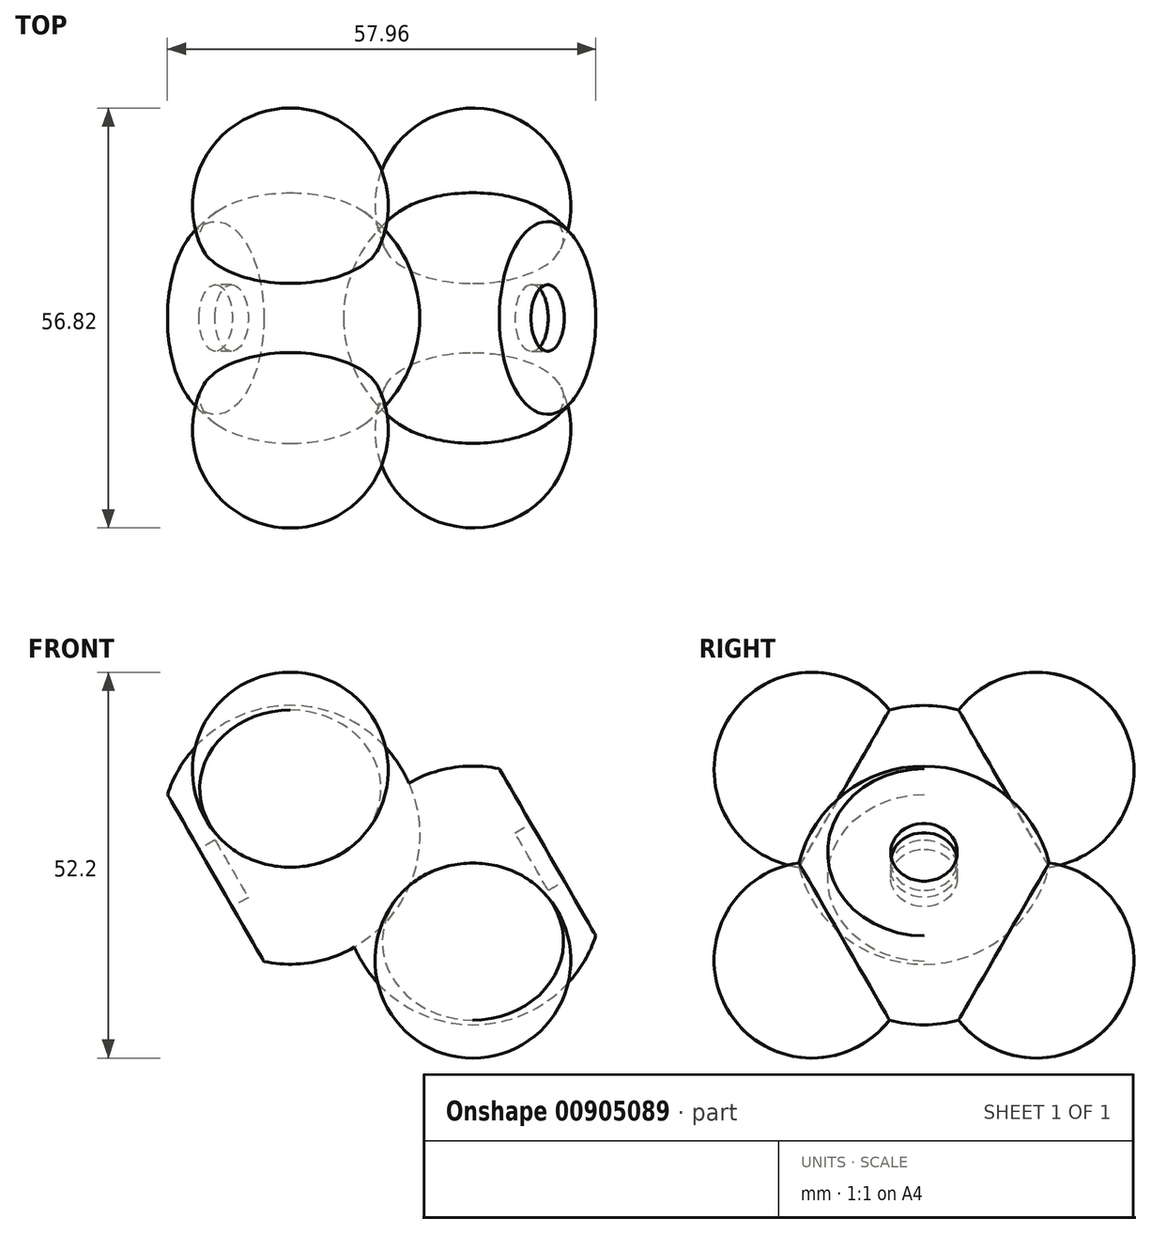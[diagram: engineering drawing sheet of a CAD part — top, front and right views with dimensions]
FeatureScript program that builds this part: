
annotation { "Feature Type Name" : "Feature", "Feature Type Description" : "" }
export const myFeature = defineFeature(function(context is Context, id is Id, definition is map)
    precondition{}
    {
        {
            var Q0;
            Q0=qCreatedBy(makeId("Front.planeOp"),FACE);
            var sketch = newSketch(context, id + "F0", { "sketchPlane" : qUnion([Q0])});
            skArc(sketch, "E0", {"start": v(-3.58, -17.13) * mm, "mid": v(15.16, 8.75) * mm, "end": v(-16.63, 5.46) * mm});
            skLineSegment(sketch, "E1", {"start": v(-16.63, 5.46) * mm, "end": v(-3.58, -17.13) * mm});
            skLineSegment(sketch, "E2", {"start": v(-10.1, -5.83) * mm, "end": v(15.16, 8.75) * mm});
            skSolve(sketch);
        }
        {
            var Q0;
            {var subQ3=sQuery(id+"F0.wireOp",EDGE,"E2");Q0=makeQuery(id+"F0.imprint","IMPRINT",FACE,{"disambiguationData":[TD([[makeQuery(id+"F0.imprint","IMPRINT",EDGE,{"derivedFrom":subQ3}),-1.0]])]});}
            var Q1;
            Q1=sQuery(id+"F0.wireOp",EDGE,"E2");
            revolve(context, id + "F1", {"surfaceOperationType" : NewSurfaceOperationType.NEW, "entities" : qUnion([Q0]), "axis" : qUnion([Q1]), "revolveType" : RevolveType.FULL});
        }
        {
            var Q0;
            Q0=qCreatedBy(makeId("Right.planeOp"),FACE);
            var sketch = newSketch(context, id + "F2", { "sketchPlane" : qUnion([Q0])});
            skCircle(sketch, "E3", {"center": v(0, 0) * mm, "radius": 17.5 * mm});
            skCircle(sketch, "E4", {"center": v(-15.16, 8.75) * mm, "radius": 13.25 * mm});
            skCircle(sketch, "E5", {"center": v(15.16, 8.75) * mm, "radius": 13.25 * mm});
            skLineSegment(sketch, "E6", {"start": v(15.16, 8.75) * mm, "end": v(0, 0) * mm});
            skLineSegment(sketch, "E7", {"start": v(-15.16, 8.75) * mm, "end": v(0, 0) * mm});
            skLineSegment(sketch, "E8", {"start": v(15.16, 8.75) * mm, "end": v(26.63, 15.37) * mm});
            skLineSegment(sketch, "E9", {"start": v(-15.16, 8.75) * mm, "end": v(-26.63, 15.38) * mm});
            skSolve(sketch);
        }
        {
            var Q0;
            {var subQ0=sQuery(id+"F2.wireOp",EDGE,"E8");Q0=makeQuery(id+"F2.imprint","IMPRINT",FACE,{"disambiguationData":[TD([[makeQuery(id+"F2.imprint","IMPRINT",EDGE,{"derivedFrom":subQ0}),1.0]])]});}
            var Q1;
            Q1=sQuery(id+"F2.wireOp",EDGE,"E8");
            revolve(context, id + "F3", {"operationType" : NewBodyOperationType.ADD, "surfaceOperationType" : NewSurfaceOperationType.NEW, "entities" : qUnion([Q0]), "axis" : qUnion([Q1]), "revolveType" : RevolveType.FULL});
        }
        {
            var Q0;
            {var subQ0=sQuery(id+"F2.wireOp",EDGE,"E9");Q0=makeQuery(id+"F2.imprint","IMPRINT",FACE,{"disambiguationData":[TD([[makeQuery(id+"F2.imprint","IMPRINT",EDGE,{"derivedFrom":subQ0}),-1.0]])]});}
            var Q1;
            Q1=sQuery(id+"F2.wireOp",EDGE,"E9");
            revolve(context, id + "F4", {"operationType" : NewBodyOperationType.ADD, "surfaceOperationType" : NewSurfaceOperationType.NEW, "entities" : qUnion([Q0]), "axis" : qUnion([Q1]), "revolveType" : RevolveType.FULL});
        }
        {
            var Q0;
            Q0=makeQuery(id+"F1.opRevolve","SWEPT_FACE",FACE,{"disambiguationData":[OSD([sQuery(id+"F0.wireOp",EDGE,"E1")])]});
            var sketch = newSketch(context, id + "F5", { "sketchPlane" : qUnion([Q0])});
            skCircle(sketch, "E10", {"center": v(0, 0) * mm, "radius": 4.5 * mm});
            skSolve(sketch);
        }
        {
            var Q0;
            Q0=makeQuery(id+"F5.imprint","IMPRINT",FACE,{"disambiguationData":[TD([[makeQuery(id+"F5.imprint","IMPRINT",EDGE,{"derivedFrom":sQuery(id+"F5.wireOp",EDGE,"E10")}),1.0]])]});
            extrude(context, id + "F6", {"entities" : qUnion([Q0]), "operationType" : NewBodyOperationType.REMOVE, "oppositeDirection" : true, "depth" : 2.5 * mm, "offsetDistance" : 25 * mm});
        }
        {
            var Q0;
            Q0=makeQuery(id+"F1.opRevolve","SWEPT_BODY",BODY,{"disambiguationData":[OSD([sQuery(id+"F0.wireOp",EDGE,"E0"),sQuery(id+"F0.wireOp",EDGE,"E1"),sQuery(id+"F0.wireOp",EDGE,"E2")])]});
            var Q1;
            Q1=qCreatedBy(makeId("Right.planeOp"),FACE);
            mirror(context, id + "F7", {"entities" : qUnion([Q0]), "mirrorPlane" : qUnion([Q1])});
        }
        {
            var Q0;
            Q0=makeQuery(id+"F7.opPattern","COPY",BODY,{"derivedFrom":makeQuery(id+"F1.opRevolve","SWEPT_BODY",BODY,{"disambiguationData":[OSD([sQuery(id+"F0.wireOp",EDGE,"E0"),sQuery(id+"F0.wireOp",EDGE,"E1"),sQuery(id+"F0.wireOp",EDGE,"E2")])]}),"instanceName":"1"});
            var Q1;
            Q1=qCreatedBy(makeId("Top.planeOp"),FACE);
            mirror(context, id + "F8", {"entities" : qUnion([Q0]), "mirrorPlane" : qUnion([Q1])});
        }
        {
            var Q0;
            Q0=makeQuery(id+"F8.opPattern","COPY",BODY,{"derivedFrom":makeQuery(id+"F7.opPattern","COPY",BODY,{"derivedFrom":makeQuery(id+"F1.opRevolve","SWEPT_BODY",BODY,{"disambiguationData":[OSD([sQuery(id+"F0.wireOp",EDGE,"E0"),sQuery(id+"F0.wireOp",EDGE,"E1"),sQuery(id+"F0.wireOp",EDGE,"E2")])]}),"instanceName":"1"}),"instanceName":"1"});
            transform(context, id + "F9", {"entities" : qUnion([Q0]), "transformType" : TransformType.TRANSLATION_3D, "dx" : 24.7 * mm, "dy" : 0 * mm, "dz" : -8.2 * mm, "makeCopy" : false});
        }
        {
            var Q0;
            Q0=makeQuery(id+"F7.opPattern","COPY",BODY,{"derivedFrom":makeQuery(id+"F1.opRevolve","SWEPT_BODY",BODY,{"disambiguationData":[OSD([sQuery(id+"F0.wireOp",EDGE,"E0"),sQuery(id+"F0.wireOp",EDGE,"E1"),sQuery(id+"F0.wireOp",EDGE,"E2")])]}),"instanceName":"1"});
            deleteBodies(context, id + "F10", {"entities" : qUnion([Q0])});
        }
    });
